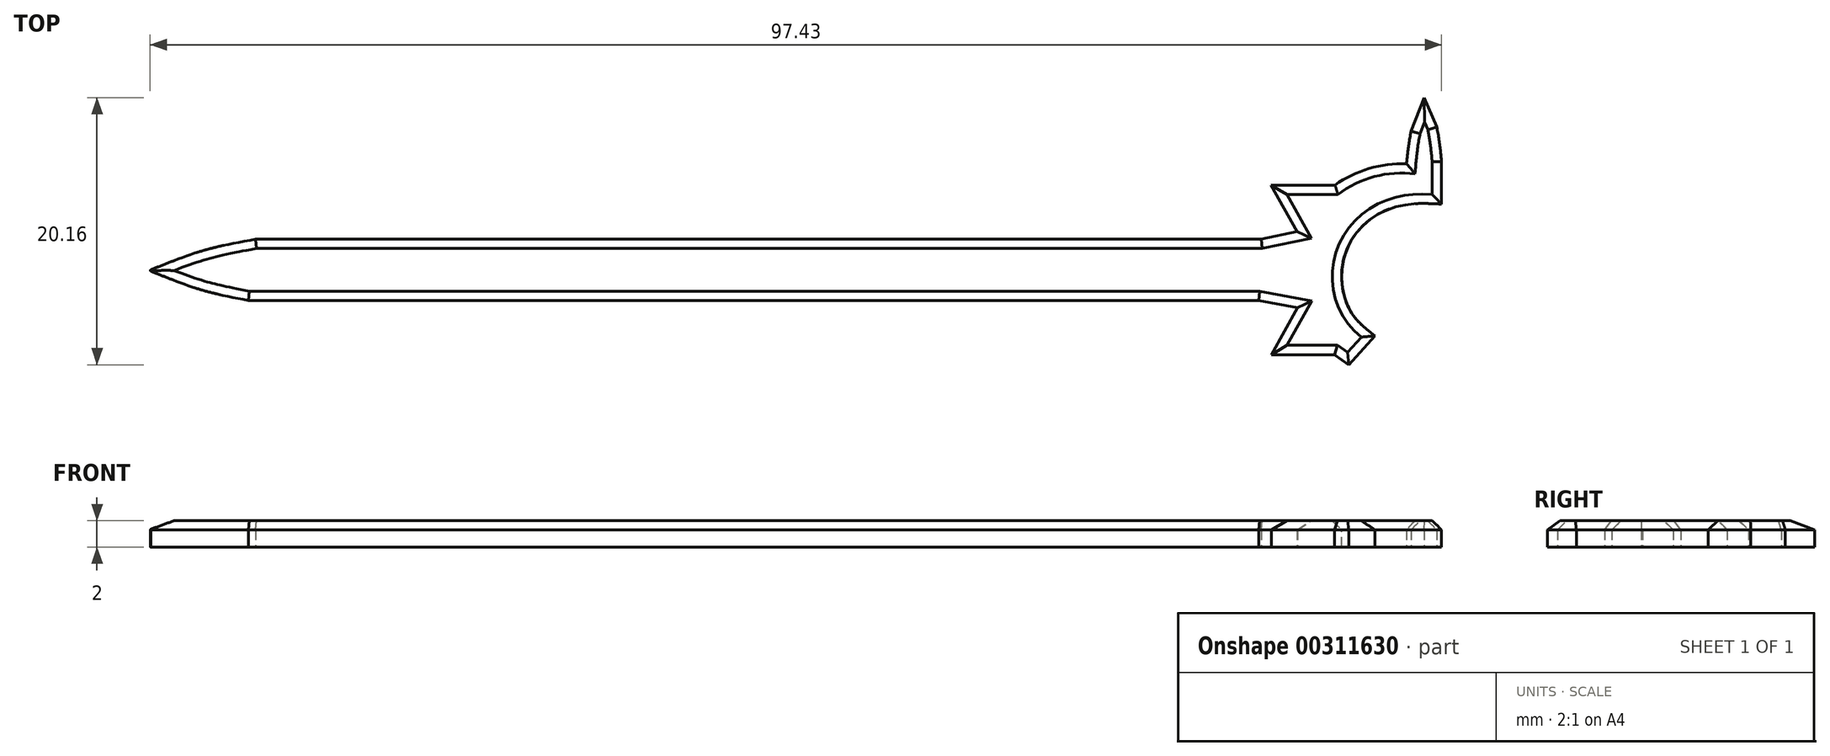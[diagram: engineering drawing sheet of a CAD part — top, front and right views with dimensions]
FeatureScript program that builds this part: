
annotation { "Feature Type Name" : "Feature", "Feature Type Description" : "" }
export const myFeature = defineFeature(function(context is Context, id is Id, definition is map)
    precondition{}
    {
        {
            var Q0;
            Q0=qCreatedBy(makeId("Top.planeOp"),FACE);
            var sketch = newSketch(context, id + "F0", { "sketchPlane" : qUnion([Q0])});
            skLineSegment(sketch, "E0", {"start": v(-51, 9.48) * mm, "end": v(24.9, 9.48) * mm});
            skLineSegment(sketch, "E1", {"start": v(24.9, 9.48) * mm, "end": v(27.59, 10.05) * mm});
            skLineSegment(sketch, "E2", {"start": v(27.59, 10.05) * mm, "end": v(25.62, 13.57) * mm});
            skLineSegment(sketch, "E3", {"start": v(25.62, 13.57) * mm, "end": v(30.45, 13.57) * mm});
            skLineSegment(sketch, "E4", {"start": v(-51.1, 4.86) * mm, "end": v(24.7, 4.86) * mm});
            skLineSegment(sketch, "E5", {"start": v(24.7, 4.86) * mm, "end": v(27.62, 4.31) * mm});
            skLineSegment(sketch, "E6", {"start": v(27.62, 4.31) * mm, "end": v(25.64, 0.77) * mm});
            skLineSegment(sketch, "E7", {"start": v(25.64, 0.77) * mm, "end": v(30.4, 0.77) * mm});
            skLineSegment(sketch, "E8", {"start": v(30.4, 0.77) * mm, "end": v(31.48, 0) * mm});
            skLineSegment(sketch, "E9", {"start": v(31.48, 0) * mm, "end": v(33.46, 2.18) * mm});
            skFitSpline(sketch, "E10", {"points": [v(33.46, 2.18) * mm, v(31.7, 3.91) * mm, v(30.95, 7.08) * mm, v(32.36, 10.3) * mm, v(35.32, 12) * mm, v(38.48, 12.13) * mm], "startDerivative": vector(-10.91, 8.41) * mm, "endDerivative": vector(15.8, -0.85) * mm});
            skArc(sketch, "E11", {"start": v(35.85, 15.17) * mm, "mid": v(33.01, 14.81) * mm, "end": v(30.45, 13.57) * mm});
            skLineSegment(sketch, "E12", {"start": v(38.48, 12.13) * mm, "end": v(38.48, 15.34) * mm});
            skFitSpline(sketch, "E13", {"points": [v(38.48, 15.34) * mm, v(38.08, 18.12) * mm, v(37.18, 20.16) * mm, v(36.2, 17.63) * mm, v(35.85, 15.17) * mm], "startDerivative": vector(-0.91, 9.82) * mm, "endDerivative": vector(-0.82, -8.71) * mm});
            skFitSpline(sketch, "E14", {"points": [v(-51, 9.48) * mm, v(-54.5, 8.75) * mm, v(-56.85, 7.98) * mm, v(-58.9, 7.17) * mm], "startDerivative": vector(-9.65, -1.8) * mm, "endDerivative": vector(-6.83, -2.74) * mm});
            skFitSpline(sketch, "E15.MirrorCS", {"points": [v(-51, 4.76) * mm, v(-54.5, 5.5) * mm, v(-56.85, 6.26) * mm, v(-58.9, 7.07) * mm], "startDerivative": vector(-9.65, 1.8) * mm, "endDerivative": vector(-6.83, 2.74) * mm});
            skLineSegment(sketch, "E16", {"start": v(-51.1, 4.86) * mm, "end": v(-51.54, 4.86) * mm});
            skFitSpline(sketch, "E17", {"points": [v(-58.9, 7.17) * mm, v(-58.95, 7.12) * mm, v(-58.9, 7.07) * mm], "startDerivative": vector(-0.11, -0.1) * mm, "endDerivative": vector(0.1, -0.1) * mm});
            skLineSegment(sketch, "E18", {"start": v(36.2, 17.63) * mm, "end": v(37.18, 20.16) * mm});
            skLineSegment(sketch, "E19", {"start": v(37.18, 20.16) * mm, "end": v(38.12, 17.95) * mm});
            skSolve(sketch);
        }
        {
            var Q0;
            Q0=makeQuery(id+"F0.imprint","IMPRINT",FACE,{"disambiguationData":[TD([[makeQuery(id+"F0.imprint","IMPRINT",EDGE,{"derivedFrom":sQuery(id+"F0.wireOp",EDGE,"E0")}),-1.0]])]});
            extrude(context, id + "F1", {"entities" : qUnion([Q0]), "depth" : 2 * mm});
        }
        {
            var Q0;
            Q0=makeQuery(id+"F1.opExtrude","CAP_EDGE",EDGE,{"disambiguationData":[OSD([sQuery(id+"F0.wireOp",EDGE,"E0")])],"isStart":false});
            var Q1;
            Q1=makeQuery(id+"F1.opExtrude","CAP_EDGE",EDGE,{"disambiguationData":[OSD([sQuery(id+"F0.wireOp",EDGE,"E14")])],"isStart":false});
            var Q2;
            Q2=makeQuery(id+"F1.opExtrude","CAP_EDGE",EDGE,{"disambiguationData":[OSD([sQuery(id+"F0.wireOp",EDGE,"E15.MirrorCS")])],"isStart":false});
            var Q3;
            Q3=makeQuery(id+"F1.opExtrude","CAP_EDGE",EDGE,{"disambiguationData":[OSD([sQuery(id+"F0.wireOp",EDGE,"E4")])],"isStart":false});
            var Q4;
            Q4=makeQuery(id+"F1.opExtrude","CAP_EDGE",EDGE,{"disambiguationData":[OSD([sQuery(id+"F0.wireOp",EDGE,"E5")])],"isStart":false});
            var Q5;
            Q5=makeQuery(id+"F1.opExtrude","CAP_EDGE",EDGE,{"disambiguationData":[OSD([sQuery(id+"F0.wireOp",EDGE,"E1")])],"isStart":false});
            var Q6;
            Q6=makeQuery(id+"F1.opExtrude","CAP_EDGE",EDGE,{"disambiguationData":[OSD([sQuery(id+"F0.wireOp",EDGE,"E2")])],"isStart":false});
            var Q7;
            Q7=makeQuery(id+"F1.opExtrude","CAP_EDGE",EDGE,{"disambiguationData":[OSD([sQuery(id+"F0.wireOp",EDGE,"E3")])],"isStart":false});
            var Q8;
            Q8=makeQuery(id+"F1.opExtrude","CAP_EDGE",EDGE,{"disambiguationData":[OSD([sQuery(id+"F0.wireOp",EDGE,"E6")])],"isStart":false});
            var Q9;
            Q9=makeQuery(id+"F1.opExtrude","CAP_EDGE",EDGE,{"disambiguationData":[OSD([sQuery(id+"F0.wireOp",EDGE,"E7")])],"isStart":false});
            var Q10;
            Q10=makeQuery(id+"F1.opExtrude","CAP_EDGE",EDGE,{"disambiguationData":[OSD([sQuery(id+"F0.wireOp",EDGE,"E8")])],"isStart":false});
            var Q11;
            Q11=makeQuery(id+"F1.opExtrude","CAP_EDGE",EDGE,{"disambiguationData":[OSD([sQuery(id+"F0.wireOp",EDGE,"E9")])],"isStart":false});
            var Q12;
            Q12=makeQuery(id+"F1.opExtrude","CAP_EDGE",EDGE,{"disambiguationData":[OSD([sQuery(id+"F0.wireOp",EDGE,"E10")])],"isStart":false});
            var Q13;
            Q13=makeQuery(id+"F1.opExtrude","CAP_EDGE",EDGE,{"disambiguationData":[OSD([sQuery(id+"F0.wireOp",EDGE,"E11")])],"isStart":false});
            var Q14;
            Q14=makeQuery(id+"F1.opExtrude","CAP_EDGE",EDGE,{"disambiguationData":[OSD([sQuery(id+"F0.wireOp",EDGE,"E12")])],"isStart":false});
            var Q15;
            Q15=makeQuery(id+"F1.opExtrude","CAP_EDGE",EDGE,{"disambiguationData":[OSD([sQuery(id+"F0.wireOp",EDGE,"E18")])],"isStart":false});
            var Q16;
            Q16=makeQuery(id+"F1.opExtrude","CAP_EDGE",EDGE,{"disambiguationData":[OSD([sQuery(id+"F0.wireOp",EDGE,"E19")])],"isStart":false});
            var Q17;
            {var subQ0=sQuery(id+"F0.wireOp",EDGE,"E13");Q17=makeQuery(id+"F1.opExtrude","CAP_EDGE",EDGE,{"disambiguationData":[OSD([subQ0]),TDD([makeQuery(id+"F0.imprint","IMPRINT",EDGE,{"disambiguationData":[TD([[makeQuery(id+"F0.imprint","INTERSECT",VERTEX,{"derivedFrom":[sQuery(id+"F0.wireOp",EDGE,"E11"),subQ0]}),1.0]])],"derivedFrom":subQ0})])],"isStart":false});}
            var Q18;
            {var subQ0=sQuery(id+"F0.wireOp",EDGE,"E13");Q18=makeQuery(id+"F1.opExtrude","CAP_EDGE",EDGE,{"disambiguationData":[OSD([subQ0]),TDD([makeQuery(id+"F0.imprint","IMPRINT",EDGE,{"disambiguationData":[TD([[makeQuery(id+"F0.imprint","INTERSECT",VERTEX,{"derivedFrom":[sQuery(id+"F0.wireOp",EDGE,"E12"),subQ0]}),-1.0]])],"derivedFrom":subQ0})])],"isStart":false});}
            chamfer(context, id + "F2", {"entities" : qUnion([Q0, Q1, Q2, Q3, Q4, Q5, Q6, Q7, Q8, Q9, Q10, Q11, Q12, Q13, Q14, Q15, Q16, Q17, Q18]), "width" : .7 * mm, "tangentPropagation" : true});
        }
    });
